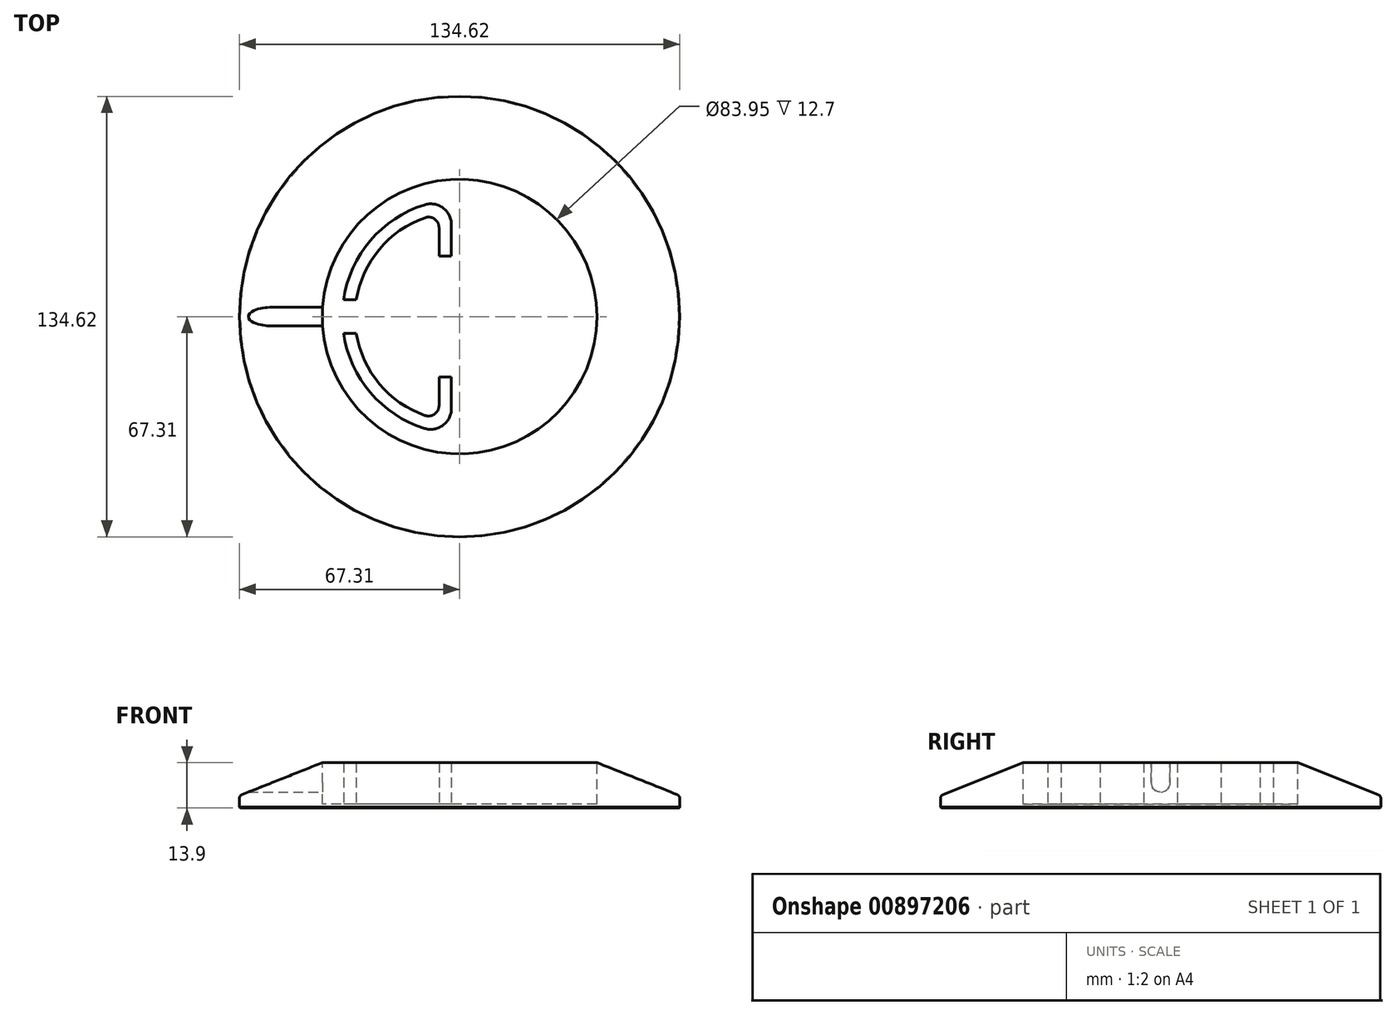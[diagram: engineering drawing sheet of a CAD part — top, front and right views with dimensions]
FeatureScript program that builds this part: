
annotation { "Feature Type Name" : "Feature", "Feature Type Description" : "" }
export const myFeature = defineFeature(function(context is Context, id is Id, definition is map)
    precondition{}
    {
        {
            var Q0;
            Q0=qCreatedBy(makeId("Front.planeOp"),FACE);
            var sketch = newSketch(context, id + "F0", { "sketchPlane" : qUnion([Q0])});
            skLineSegment(sketch, "E0", {"start": v(0, 0) * mm, "end": v(-67.31, 0) * mm});
            skLineSegment(sketch, "E1", {"start": v(-67.31, 0) * mm, "end": v(-67.31, 3.8) * mm});
            skLineSegment(sketch, "E2", {"start": v(-67.31, 3.8) * mm, "end": v(-41.97, 13.9) * mm});
            skLineSegment(sketch, "E3", {"start": v(-41.97, 13.9) * mm, "end": v(-41.97, 1.2) * mm});
            skLineSegment(sketch, "E4", {"start": v(-41.97, 1.2) * mm, "end": v(0, 1.2) * mm});
            skLineSegment(sketch, "E5", {"start": v(0, 1.2) * mm, "end": v(0, 0) * mm});
            skLineSegment(sketch, "E6", {"start": v(0, 41.52) * mm, "end": v(0, -29.14) * mm, "construction": true});
            skSolve(sketch);
        }
        {
            var Q0;
            Q0=makeQuery(id+"F0.imprint","IMPRINT",FACE,{"disambiguationData":[TD([[makeQuery(id+"F0.imprint","IMPRINT",EDGE,{"derivedFrom":sQuery(id+"F0.wireOp",EDGE,"E0")}),-1.0]])]});
            var Q1;
            Q1=sQuery(id+"F0.wireOp",EDGE,"E6");
            revolve(context, id + "F1", {"surfaceOperationType" : NewSurfaceOperationType.NEW, "entities" : qUnion([Q0]), "axis" : qUnion([Q1]), "revolveType" : RevolveType.FULL});
        }
        {
            var Q0;
            Q0=makeQuery(id+"F1.opRevolve","SWEPT_EDGE",EDGE,{"disambiguationData":[OSD([sQuery(id+"F0.wireOp",EDGE,"E1"),sQuery(id+"F0.wireOp",EDGE,"E2")])]});
            fillet(context, id + "F2", {"entities" : qUnion([Q0]), "radius" : 1.27 * mm, "tangentPropagation" : true, "allowEdgeOverflow" : false});
        }
        {
            var Q0;
            Q0=makeQuery(id+"F1.opRevolve","SWEPT_FACE",FACE,{"disambiguationData":[OSD([sQuery(id+"F0.wireOp",EDGE,"E4")])]});
            var sketch = newSketch(context, id + "F3", { "sketchPlane" : qUnion([Q0])});
            skCircle(sketch, "E7.0", {"center": v(0, 0) * mm, "radius": 41.97 * mm, "construction": true});
            skCircle(sketch, "E8.0", {"center": v(0, 0) * mm, "radius": 67.31 * mm, "construction": true});
            skLineSegment(sketch, "E9", {"start": v(0, 73.68) * mm, "end": v(0, -74.76) * mm, "construction": true});
            skLineSegment(sketch, "E10", {"start": v(-2.48, 53.7) * mm, "end": v(-2.48, 18.46) * mm, "construction": true});
            skArc(sketch, "E11", {"start": v(-35.45, -5.1) * mm, "mid": v(35.81, 0) * mm, "end": v(-35.45, 5.1) * mm, "construction": true});
            skArc(sketch, "E12", {"start": v(-10.73, 34.17) * mm, "mid": v(-27.28, 23.2) * mm, "end": v(-35.45, 5.1) * mm});
            skLineSegment(sketch, "E13", {"start": v(-2.48, 28.11) * mm, "end": v(-2.48, 18.46) * mm});
            skArc(sketch, "E14.0", {"start": v(-10.5, 30.23) * mm, "mid": v(-24.51, 20.58) * mm, "end": v(-31.6, 5.1) * mm});
            skLineSegment(sketch, "E14.1", {"start": v(-6.29, 27.23) * mm, "end": v(-6.29, 18.46) * mm});
            skPoint(sketch, "E15.visualSharp", {"position": v(-2.48, 35.73) * mm});
            skArc(sketch, "E15.filletArc", {"start": v(-2.48, 28.11) * mm, "mid": v(-5.07, 33.23) * mm, "end": v(-10.73, 34.17) * mm});
            skPoint(sketch, "E16.visualSharp", {"position": v(-2.48, -35.73) * mm});
            skArc(sketch, "E16.filletArc", {"start": v(-10.73, -34.17) * mm, "mid": v(-5.07, -33.23) * mm, "end": v(-2.48, -28.11) * mm});
            skPoint(sketch, "E17.visualSharp", {"position": v(-6.29, 31.38) * mm});
            skArc(sketch, "E17.filletArc", {"start": v(-6.29, 27.23) * mm, "mid": v(-7.62, 29.82) * mm, "end": v(-10.5, 30.23) * mm});
            skPoint(sketch, "E18.visualSharp", {"position": v(-6.29, -31.38) * mm});
            skArc(sketch, "E18.filletArc", {"start": v(-10.5, -30.23) * mm, "mid": v(-7.62, -29.82) * mm, "end": v(-6.29, -27.23) * mm});
            skLineSegment(sketch, "E19", {"start": v(-2.48, 18.46) * mm, "end": v(-6.29, 18.46) * mm});
            skLineSegment(sketch, "E20", {"start": v(4.95, 0) * mm, "end": v(-44.3, 0) * mm, "construction": true});
            skLineSegment(sketch, "E21.MirrorCS", {"start": v(-2.48, -18.46) * mm, "end": v(-6.29, -18.46) * mm});
            skPoint(sketch, "E22", {"position": v(-35.81, 0) * mm});
            skLineSegment(sketch, "E23", {"start": v(-31.6, 5.1) * mm, "end": v(-35.45, 5.1) * mm});
            skLineSegment(sketch, "E24.MirrorCS", {"start": v(-31.6, -5.1) * mm, "end": v(-35.45, -5.1) * mm});
            skLineSegment(sketch, "E25.trimOffspring", {"start": v(-2.48, -18.46) * mm, "end": v(-2.48, -57.22) * mm, "construction": true});
            skLineSegment(sketch, "E26.trimOffspring", {"start": v(-2.48, -18.46) * mm, "end": v(-2.48, -28.11) * mm});
            skLineSegment(sketch, "E27.trimOffspring", {"start": v(-6.29, -18.46) * mm, "end": v(-6.29, -27.23) * mm});
            skArc(sketch, "E28.trimOffspring", {"start": v(-31.6, -5.1) * mm, "mid": v(-24.51, -20.58) * mm, "end": v(-10.5, -30.23) * mm});
            skArc(sketch, "E29.trimOffspring", {"start": v(-35.45, -5.1) * mm, "mid": v(-27.28, -23.2) * mm, "end": v(-10.73, -34.17) * mm});
            skSolve(sketch);
        }
        {
            var Q0;
            Q0=makeQuery(id+"F3.imprint","IMPRINT",FACE,{"disambiguationData":[TD([[makeQuery(id+"F3.imprint","IMPRINT",EDGE,{"derivedFrom":sQuery(id+"F3.wireOp",EDGE,"E12")}),1.0]])]});
            var Q1;
            Q1=makeQuery(id+"F3.imprint","IMPRINT",FACE,{"disambiguationData":[TD([[makeQuery(id+"F3.imprint","IMPRINT",EDGE,{"derivedFrom":sQuery(id+"F3.wireOp",EDGE,"E16.filletArc")}),1.0]])]});
            extrude(context, id + "F4", {"entities" : qUnion([Q0, Q1]), "operationType" : NewBodyOperationType.ADD, "depth" : 12.7 * mm, "offsetDistance" : 25.4 * mm});
        }
        {
            var Q0;
            Q0=qCreatedBy(makeId("Right.planeOp"),FACE);
            var sketch = newSketch(context, id + "F5", { "sketchPlane" : qUnion([Q0])});
            skLineSegment(sketch, "E30.0", {"start": v(-41.97, 13.9) * mm, "end": v(41.97, 13.9) * mm, "construction": true});
            skLineSegment(sketch, "E31.0", {"start": v(-41.97, 1.2) * mm, "end": v(41.97, 1.2) * mm, "construction": true});
            skLineSegment(sketch, "E32", {"start": v(0, 24.44) * mm, "end": v(0, -9.72) * mm, "construction": true});
            skLineSegment(sketch, "E33", {"start": v(-2.86, 13.9) * mm, "end": v(-2.86, 7.74) * mm});
            skLineSegment(sketch, "E34.MirrorCS", {"start": v(2.86, 13.9) * mm, "end": v(2.86, 7.74) * mm});
            skLineSegment(sketch, "E35", {"start": v(-2.86, 13.9) * mm, "end": v(2.86, 13.9) * mm});
            skArc(sketch, "E36", {"start": v(-2.86, 7.74) * mm, "mid": v(0, 4.88) * mm, "end": v(2.86, 7.74) * mm});
            skSolve(sketch);
        }
        {
            var Q0;
            Q0=makeQuery(id+"F5.imprint","IMPRINT",FACE,{"disambiguationData":[TD([[makeQuery(id+"F5.imprint","IMPRINT",EDGE,{"derivedFrom":sQuery(id+"F5.wireOp",EDGE,"E33")}),1.0]])]});
            extrude(context, id + "F6", {"entities" : qUnion([Q0]), "operationType" : NewBodyOperationType.REMOVE, "oppositeDirection" : true, "depth" : 127 * mm, "offsetDistance" : 25.4 * mm});
        }
        {
            var Q0;
            Q0=makeQuery(id+"F1.opRevolve","SWEPT_EDGE",EDGE,{"disambiguationData":[OSD([sQuery(id+"F0.wireOp",EDGE,"E0"),sQuery(id+"F0.wireOp",EDGE,"E1")])]});
            chamfer(context, id + "F7", {"entities" : qUnion([Q0]), "width" : 0.25 * mm, "tangentPropagation" : true});
        }
    });
